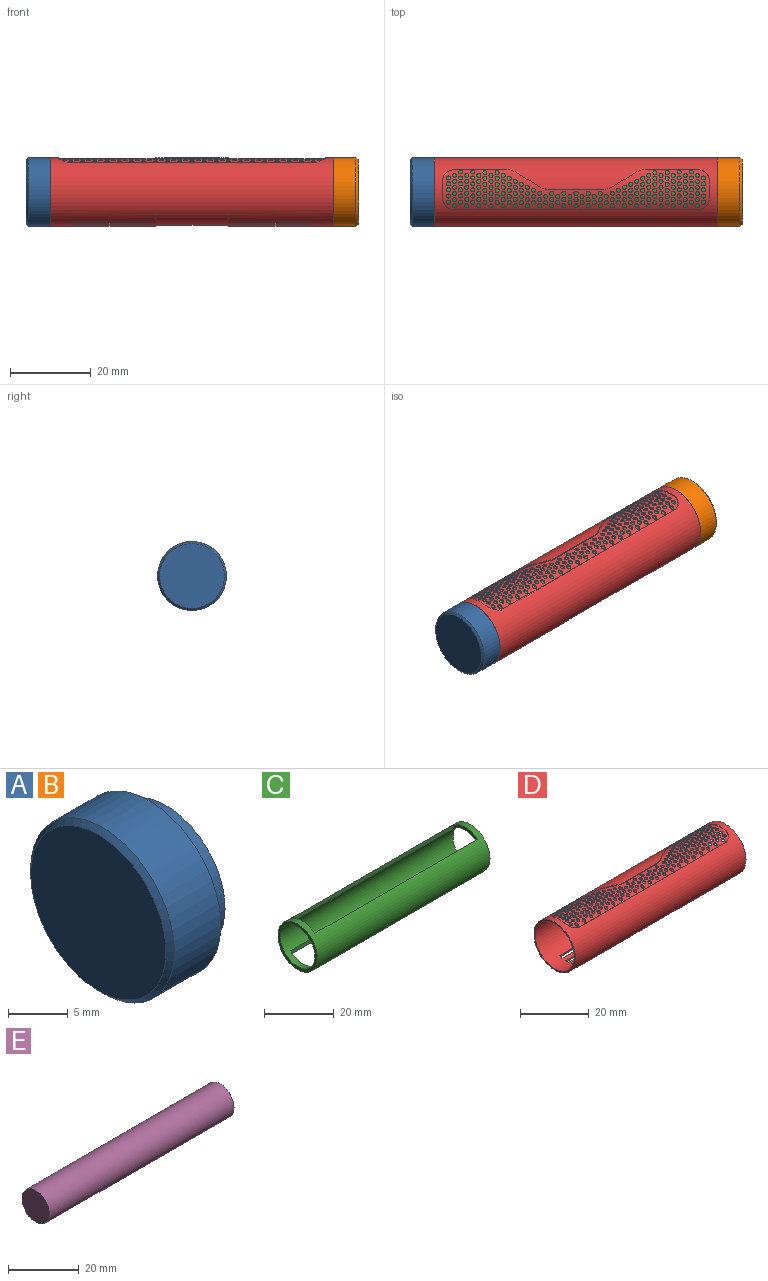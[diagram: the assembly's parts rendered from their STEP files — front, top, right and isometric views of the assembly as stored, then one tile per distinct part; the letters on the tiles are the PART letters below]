
ASSEMBLY  parts=5 mates=5
PART A: 8 faces, bbox 8x17x17 mm
  f0: cylinder r=5.5mm len=11mm, axis (-1,0,0), area 103.7mm2, adj f1,f6
  f1: plane 11x11mm, normal (1,0,0), area 95mm2, adj f0
  f2: cone r=8.25mm half-angle=45deg, axis (1,0,0), area 36.7mm2, adj f3,f4
  f3: cylinder r=8.5mm len=17mm, axis (1,0,0), area 293.7mm2, adj f2,f7
  f4: plane 16x16mm, normal (-1,0,0), area 201.1mm2, adj f2
  f5: cylinder r=7mm len=14mm, axis (1,0,0), area 88mm2, adj f6,f7
  f6: plane 14x14mm, normal (1,0,0), area 58.9mm2, adj f0,f5
  f7: plane 17x17mm, normal (1,0,0), area 73mm2, adj f3,f5
PART B: same geometry as A
PART C: 12 faces, bbox 70x16x16 mm
  f0: plane 10x3.1mm, normal (1,0,0), area 11mm2, adj f2,f4,f8,f10
  f1: plane 10x3.1mm, normal (1,0,0), area 11mm2, adj f3,f7,f8,f10
  f2: plane 66x1.35mm, normal (0,-1,0), area 88.8mm2, adj f0,f5,f8,f10
  f3: plane 66x1.35mm, normal (0,-1,0), area 88.8mm2, adj f1,f6,f8,f10
  f4: plane 66x1.35mm, normal (0,1,0), area 88.8mm2, adj f0,f5,f8,f10
  f5: plane 10x3.1mm, normal (-1,0,0), area 11mm2, adj f2,f4,f8,f10
  f6: plane 10x3.1mm, normal (-1,0,0), area 11mm2, adj f3,f7,f8,f10
  f7: plane 66x1.35mm, normal (0,1,0), area 88.8mm2, adj f1,f6,f8,f10
  f8: cylinder r=7mm len=70mm, axis (1,0,0), area 1608.5mm2, adj f0,f1,f2,f3,f4,f5,f6,f7
  f9: plane 16x16mm, normal (-1,0,0), area 47.1mm2, adj f8,f10
  f10: cylinder r=8mm len=70mm, axis (1,0,0), area 2092.7mm2, adj f0,f1,f2,f3,f4,f5,f6,f7
  f11: plane 16x16mm, normal (1,0,0), area 47.1mm2, adj f8,f10
PART D: 246 faces, bbox 70.2x17.2x17.2 mm
  f0: plane 13.02x3.2mm, normal (1,0,0), area 3.7mm2, adj f1,f2,f3,f244
  f1: plane 18x0.19mm, normal (0,0.64,-0.77), area 4.5mm2, adj f0,f2,f4,f244
  f2: cylinder r=8.25mm len=18mm, axis (1,0,0), area 259.2mm2, adj f0,f1,f3,f4
  f3: plane 18x0.19mm, normal (0,-0.64,-0.77), area 4.5mm2, adj f0,f2,f4,f244
  f4: plane 13.02x3.2mm, normal (-1,0,0), area 3.7mm2, adj f1,f2,f3,f244
  f5: plane 1x0.85mm, normal (1,0,0), area 0.5mm2, adj f6,f8,f128,f244
  f6: plane 20x0.52mm, normal (0,1,0), area 10.3mm2, adj f5,f7,f128,f244
  f7: plane 1x0.85mm, normal (-1,0,0), area 0.5mm2, adj f6,f8,f128,f244
  f8: plane 20x0.54mm, normal (0,-1,0), area 10.7mm2, adj f5,f7,f128,f244
  f9: plane 1x0.85mm, normal (1,0,0), area 0.5mm2, adj f10,f12,f128,f244
  f10: plane 20x0.54mm, normal (0,1,0), area 10.7mm2, adj f9,f11,f128,f244
  f11: plane 1x0.85mm, normal (-1,0,0), area 0.5mm2, adj f10,f12,f128,f244
  f12: plane 20x0.52mm, normal (0,-1,0), area 10.3mm2, adj f9,f11,f128,f244
  f13: plane 20x0.5mm, normal (0,1,0), area 10mm2, adj f14,f16,f128,f244
  f14: plane 1x0.52mm, normal (1,0,0), area 0.5mm2, adj f13,f15,f128,f244
  f15: plane 20x0.5mm, normal (0,-1,0), area 10mm2, adj f14,f16,f128,f244
  f16: plane 1x0.52mm, normal (-1,0,0), area 0.5mm2, adj f13,f15,f128,f244
  f17: plane 1x0.85mm, normal (-1,0,0), area 0.5mm2, adj f18,f20,f128,f244
  f18: plane 20x0.52mm, normal (0,1,0), area 10.3mm2, adj f17,f19,f128,f244
  f19: plane 1x0.85mm, normal (1,0,0), area 0.5mm2, adj f18,f20,f128,f244
  f20: plane 20x0.54mm, normal (0,-1,0), area 10.7mm2, adj f17,f19,f128,f244
  f21: plane 1x0.52mm, normal (1,0,0), area 0.5mm2, adj f22,f24,f128,f244
  f22: plane 20x0.5mm, normal (0,-1,0), area 10mm2, adj f21,f23,f128,f244
  f23: plane 1x0.52mm, normal (-1,0,0), area 0.5mm2, adj f22,f24,f128,f244
  f24: plane 20x0.5mm, normal (0,1,0), area 10mm2, adj f21,f23,f128,f244
  f25: plane 1x0.85mm, normal (-1,0,0), area 0.5mm2, adj f26,f28,f128,f244
  f26: plane 20x0.54mm, normal (0,1,0), area 10.7mm2, adj f25,f27,f128,f244
  f27: plane 1x0.85mm, normal (1,0,0), area 0.5mm2, adj f26,f28,f128,f244
  f28: plane 20x0.52mm, normal (0,-1,0), area 10.3mm2, adj f25,f27,f128,f244
  f29: cylinder r=0.5mm len=1mm, axis (0,0,-1), area 0.8mm2, adj f127,f128
  f30: cylinder r=0.5mm len=1mm, axis (0,0,-1), area 0.8mm2, adj f127,f128
  f31: cylinder r=0.5mm len=1mm, axis (0,0,-1), area 0.8mm2, adj f127,f128
  f32: cylinder r=0.5mm len=1mm, axis (0,0,-1), area 0.9mm2, adj f127,f128
  f33: cylinder r=0.5mm len=1mm, axis (0,0,-1), area 0.8mm2, adj f127,f128
  f34: cylinder r=0.5mm len=1mm, axis (0,0,-1), area 0.7mm2, adj f127,f128
  f35: cylinder r=0.5mm len=1mm, axis (0,0,-1), area 0.9mm2, adj f127,f128
  f36: cylinder r=0.5mm len=1mm, axis (0,0,-1), area 0.8mm2, adj f127,f128
  f37: cylinder r=0.5mm len=1mm, axis (0,0,-1), area 0.8mm2, adj f127,f128
  f38: cylinder r=0.5mm len=1mm, axis (0,0,-1), area 1mm2, adj f127,f128
  f39: cylinder r=0.5mm len=1mm, axis (0,0,-1), area 0.8mm2, adj f127,f128
  f40: cylinder r=0.5mm len=1mm, axis (0,0,-1), area 0.7mm2, adj f127,f128
  f41: cylinder r=0.5mm len=1mm, axis (0,0,-1), area 0.9mm2, adj f127,f128
  f42: cylinder r=0.5mm len=1mm, axis (0,0,-1), area 0.8mm2, adj f127,f128
  f43: cylinder r=0.5mm len=1mm, axis (0,0,-1), area 0.8mm2, adj f127,f128
  f44: cylinder r=0.5mm len=1mm, axis (0,0,-1), area 1mm2, adj f127,f128
  f45: cylinder r=0.5mm len=1mm, axis (0,0,-1), area 0.8mm2, adj f127,f128
  f46: cylinder r=0.5mm len=1mm, axis (0,0,-1), area 0.7mm2, adj f127,f128
  f47: cylinder r=0.5mm len=1mm, axis (0,0,-1), area 0.9mm2, adj f127,f128
  f48: cylinder r=0.5mm len=1mm, axis (0,0,-1), area 0.8mm2, adj f127,f128
  f49: cylinder r=0.5mm len=1mm, axis (0,0,-1), area 0.8mm2, adj f127,f128
  f50: cylinder r=0.5mm len=1mm, axis (0,0,-1), area 1mm2, adj f127,f128
  f51: cylinder r=0.5mm len=1mm, axis (0,0,-1), area 0.9mm2, adj f127,f128
  f52: cylinder r=0.5mm len=1mm, axis (0,0,-1), area 0.7mm2, adj f127,f128
  f53: cylinder r=0.5mm len=1mm, axis (0,0,-1), area 0.9mm2, adj f127,f128
  f54: cylinder r=0.5mm len=1mm, axis (0,0,-1), area 0.8mm2, adj f127,f128
  f55: cylinder r=0.5mm len=1mm, axis (0,0,-1), area 0.8mm2, adj f127,f128
  f56: cylinder r=0.5mm len=1mm, axis (0,0,-1), area 1mm2, adj f127,f128
  f57: cylinder r=0.5mm len=1mm, axis (0,0,-1), area 0.8mm2, adj f127,f128
  f58: cylinder r=0.5mm len=1mm, axis (0,0,-1), area 1mm2, adj f127,f128
  f59: cylinder r=0.5mm len=1mm, axis (0,0,-1), area 0.9mm2, adj f127,f128
  f60: cylinder r=0.5mm len=1mm, axis (0,0,-1), area 0.8mm2, adj f127,f128
  f61: cylinder r=0.5mm len=1mm, axis (0,0,-1), area 0.8mm2, adj f127,f128
  f62: cylinder r=0.5mm len=1mm, axis (0,0,-1), area 0.8mm2, adj f127,f128
  f63: cylinder r=0.5mm len=1mm, axis (0,0,-1), area 0.9mm2, adj f127,f128
  f64: cylinder r=0.5mm len=1mm, axis (0,0,-1), area 0.7mm2, adj f127,f128
  f65: cylinder r=0.5mm len=1mm, axis (0,0,-1), area 0.8mm2, adj f127,f128
  f66: cylinder r=0.5mm len=1mm, axis (0,0,-1), area 0.8mm2, adj f127,f128
  f67: cylinder r=0.5mm len=1mm, axis (0,0,-1), area 0.9mm2, adj f127,f128
  f68: cylinder r=0.5mm len=1mm, axis (0,0,-1), area 0.7mm2, adj f127,f128
  f69: cylinder r=0.5mm len=1mm, axis (0,0,-1), area 0.8mm2, adj f127,f128
  f70: cylinder r=0.5mm len=1mm, axis (0,0,-1), area 1mm2, adj f127,f128
  f71: cylinder r=0.5mm len=1mm, axis (0,0,-1), area 0.9mm2, adj f127,f128
  f72: cylinder r=0.5mm len=1mm, axis (0,0,-1), area 0.8mm2, adj f127,f128
  f73: cylinder r=0.5mm len=1mm, axis (0,0,-1), area 1mm2, adj f127,f128
  f74: cylinder r=0.5mm len=1mm, axis (0,0,-1), area 0.9mm2, adj f127,f128
  f75: cylinder r=0.5mm len=1mm, axis (0,0,-1), area 1mm2, adj f127,f128
  f76: cylinder r=0.5mm len=1mm, axis (0,0,-1), area 0.9mm2, adj f127,f128
  f77: cylinder r=0.5mm len=1mm, axis (0,0,-1), area 0.8mm2, adj f127,f128
  f78: cylinder r=0.5mm len=1mm, axis (0,0,-1), area 0.4mm2, adj f127,f128,f178
  f79: cylinder r=0.5mm len=1mm, axis (0,0,-1), area 0.4mm2, adj f127,f128,f177
  f80: cylinder r=0.5mm len=1mm, axis (0,0,-1), area 0.5mm2, adj f127,f128,f176
  f81: cylinder r=0.5mm len=1mm, axis (0,0,-1), area 0.9mm2, adj f127,f128
  f82: cylinder r=0.5mm len=1mm, axis (0,0,-1), area 0.9mm2, adj f127,f128
  f83: cylinder r=0.5mm len=1mm, axis (0,0,-1), area 0.8mm2, adj f127,f128
  f84: cylinder r=0.5mm len=1mm, axis (0,0,-1), area 0.9mm2, adj f127,f128
  f85: cylinder r=0.5mm len=1mm, axis (0,0,-1), area 0.8mm2, adj f127,f128
  f86: cylinder r=0.5mm len=1mm, axis (0,0,-1), area 0.9mm2, adj f127,f128
  f87: cylinder r=0.5mm len=1mm, axis (0,0,-1), area 0.9mm2, adj f127,f128
  f88: cylinder r=0.5mm len=1mm, axis (0,0,-1), area 0.8mm2, adj f127,f128
  f89: cylinder r=0.5mm len=1mm, axis (0,0,-1), area 0.9mm2, adj f127,f128
  f90: cylinder r=0.5mm len=1mm, axis (0,0,-1), area 1mm2, adj f127,f128
  f91: cylinder r=0.5mm len=1mm, axis (0,0,-1), area 0.9mm2, adj f127,f128
  f92: cylinder r=0.5mm len=1mm, axis (0,0,-1), area 0.8mm2, adj f127,f128
  f93: cylinder r=0.5mm len=1mm, axis (0,0,-1), area 0.9mm2, adj f127,f128
  f94: cylinder r=0.5mm len=1mm, axis (0,0,-1), area 1mm2, adj f127,f128
  f95: cylinder r=0.5mm len=1mm, axis (0,0,-1), area 0.9mm2, adj f127,f128
  f96: cylinder r=0.5mm len=1mm, axis (0,0,-1), area 0.9mm2, adj f127,f128
  f97: cylinder r=0.5mm len=1mm, axis (0,0,-1), area 0.8mm2, adj f127,f128
  f98: cylinder r=0.5mm len=1mm, axis (0,0,-1), area 0.9mm2, adj f127,f128
  f99: cylinder r=0.5mm len=1mm, axis (0,0,-1), area 0.9mm2, adj f127,f128
  f100: cylinder r=0.5mm len=1mm, axis (0,0,-1), area 0.7mm2, adj f127,f128
  f101: cylinder r=0.5mm len=1mm, axis (0,0,-1), area 0.8mm2, adj f127,f128
  f102: cylinder r=0.5mm len=1mm, axis (0,0,-1), area 0.9mm2, adj f127,f128
  f103: cylinder r=0.5mm len=1mm, axis (0,0,-1), area 0.8mm2, adj f127,f128
  f104: cylinder r=0.5mm len=1mm, axis (0,0,-1), area 0.9mm2, adj f127,f128
  f105: cylinder r=0.5mm len=1mm, axis (0,0,-1), area 0.8mm2, adj f127,f128
  f106: cylinder r=0.5mm len=1mm, axis (0,0,-1), area 1mm2, adj f127,f128
  f107: cylinder r=0.5mm len=1mm, axis (0,0,-1), area 0.9mm2, adj f127,f128
  f108: cylinder r=0.5mm len=1mm, axis (0,0,-1), area 0.9mm2, adj f127,f128
  f109: cylinder r=0.5mm len=1mm, axis (0,0,-1), area 0.8mm2, adj f127,f128
  f110: cylinder r=0.5mm len=1mm, axis (0,0,-1), area 0.9mm2, adj f127,f128
  f111: cylinder r=0.5mm len=1mm, axis (0,0,-1), area 0.8mm2, adj f127,f128
  f112: cylinder r=0.5mm len=1mm, axis (0,0,-1), area 1mm2, adj f127,f128
  f113: cylinder r=0.5mm len=1mm, axis (0,0,-1), area 0.9mm2, adj f127,f128
  f114: cylinder r=0.5mm len=1mm, axis (0,0,-1), area 0.9mm2, adj f127,f128
  f115: cylinder r=0.5mm len=1mm, axis (0,0,-1), area 0.8mm2, adj f127,f128
  f116: cylinder r=0.5mm len=1mm, axis (0,0,-1), area 0.8mm2, adj f127,f128
  f117: cylinder r=0.5mm len=1mm, axis (0,0,-1), area 0.8mm2, adj f127,f128
  f118: cylinder r=0.5mm len=1mm, axis (0,0,-1), area 1mm2, adj f127,f128
  f119: cylinder r=0.5mm len=1mm, axis (0,0,-1), area 0.9mm2, adj f127,f128
  f120: cylinder r=0.5mm len=1mm, axis (0,0,-1), area 0.9mm2, adj f127,f128
  f121: cylinder r=0.5mm len=1mm, axis (0,0,-1), area 0.8mm2, adj f127,f128
  f122: cylinder r=0.5mm len=1mm, axis (0,0,-1), area 0.8mm2, adj f127,f128
  f123: cylinder r=0.5mm len=1mm, axis (0,0,-1), area 0.8mm2, adj f127,f128
  f124: cylinder r=0.5mm len=1mm, axis (0,0,-1), area 1mm2, adj f127,f128
  f125: cylinder r=0.5mm len=1mm, axis (0,0,-1), area 0.9mm2, adj f127,f128
  f126: cylinder r=0.5mm len=1mm, axis (0,0,-1), area 0.8mm2, adj f127,f128
  f127: cylinder r=8.25mm len=66mm, axis (-1,0,0), area 409.4mm2, adj f29,f30,f31,f32,f33,f34,f35,f36
  f128: cylinder r=8mm len=70mm, axis (1,0,0), area 3233.7mm2, adj f5,f6,f7,f8,f9,f10,f11,f12
  f129: cylinder r=0.5mm len=1mm, axis (0,0,1), area 0.8mm2, adj f127,f128
  f130: cylinder r=0.5mm len=1mm, axis (0,0,1), area 0.8mm2, adj f127,f128
  f131: cylinder r=0.5mm len=1mm, axis (0,0,1), area 0.9mm2, adj f127,f128
  f132: cylinder r=0.5mm len=1mm, axis (0,0,1), area 1mm2, adj f127,f128
  f133: cylinder r=0.5mm len=1mm, axis (0,0,1), area 0.8mm2, adj f127,f128
  f134: cylinder r=0.5mm len=1mm, axis (0,0,1), area 0.9mm2, adj f127,f128
  f135: cylinder r=0.5mm len=1mm, axis (0,0,1), area 0.8mm2, adj f127,f128
  f136: cylinder r=0.5mm len=1mm, axis (0,0,1), area 0.9mm2, adj f127,f128
  f137: cylinder r=0.5mm len=1mm, axis (0,0,1), area 0.9mm2, adj f127,f128
  f138: cylinder r=0.5mm len=1mm, axis (0,0,1), area 1mm2, adj f127,f128
  f139: cylinder r=0.5mm len=1mm, axis (0,0,1), area 0.8mm2, adj f127,f128
  f140: cylinder r=0.5mm len=1mm, axis (0,0,1), area 0.8mm2, adj f127,f128
  f141: cylinder r=0.5mm len=1mm, axis (0,0,1), area 0.8mm2, adj f127,f128
  f142: cylinder r=0.5mm len=1mm, axis (0,0,1), area 0.8mm2, adj f127,f128
  f143: cylinder r=0.5mm len=1mm, axis (0,0,1), area 0.9mm2, adj f127,f128
  f144: cylinder r=0.5mm len=1mm, axis (0,0,1), area 1mm2, adj f127,f128
  f145: cylinder r=0.5mm len=1mm, axis (0,0,1), area 0.8mm2, adj f127,f128
  f146: cylinder r=0.5mm len=1mm, axis (0,0,1), area 0.8mm2, adj f127,f128
  f147: cylinder r=0.5mm len=1mm, axis (0,0,1), area 0.8mm2, adj f127,f128
  f148: cylinder r=0.5mm len=1mm, axis (0,0,1), area 0.8mm2, adj f127,f128
  f149: cylinder r=0.5mm len=1mm, axis (0,0,1), area 0.9mm2, adj f127,f128
  f150: cylinder r=0.5mm len=1mm, axis (0,0,1), area 1mm2, adj f127,f128
  f151: cylinder r=0.5mm len=1mm, axis (0,0,1), area 0.8mm2, adj f127,f128
  f152: cylinder r=0.5mm len=1mm, axis (0,0,1), area 0.8mm2, adj f127,f128
  f153: cylinder r=0.5mm len=1mm, axis (0,0,1), area 0.8mm2, adj f127,f128
  f154: cylinder r=0.5mm len=1mm, axis (0,0,1), area 0.8mm2, adj f127,f128
  f155: cylinder r=0.5mm len=1mm, axis (0,0,1), area 0.8mm2, adj f127,f128
  f156: cylinder r=0.5mm len=1mm, axis (0,0,1), area 0.7mm2, adj f127,f128
  f157: cylinder r=0.5mm len=1mm, axis (0,0,1), area 0.8mm2, adj f127,f128
  f158: cylinder r=0.5mm len=1mm, axis (0,0,1), area 0.8mm2, adj f127,f128
  f159: cylinder r=0.5mm len=1mm, axis (0,0,1), area 0.8mm2, adj f127,f128
  f160: cylinder r=0.5mm len=1mm, axis (0,0,1), area 0.8mm2, adj f127,f128
  f161: cylinder r=0.5mm len=1mm, axis (0,0,1), area 0.9mm2, adj f127,f128
  f162: cylinder r=0.5mm len=1mm, axis (0,0,1), area 1mm2, adj f127,f128
  f163: cylinder r=0.5mm len=1mm, axis (0,0,1), area 0.9mm2, adj f127,f128
  f164: cylinder r=0.5mm len=1mm, axis (0,0,1), area 0.8mm2, adj f127,f128
  f165: cylinder r=0.5mm len=1mm, axis (0,0,1), area 0.9mm2, adj f127,f128
  f166: cylinder r=0.5mm len=1mm, axis (0,0,1), area 1mm2, adj f127,f128
  f167: cylinder r=0.5mm len=1mm, axis (0,0,1), area 0.9mm2, adj f127,f128
  f168: cylinder r=0.5mm len=1mm, axis (0,0,1), area 0.8mm2, adj f127,f128
  f169: cylinder r=0.5mm len=1mm, axis (0,0,1), area 0.9mm2, adj f127,f128
  f170: cylinder r=0.5mm len=1mm, axis (0,0,1), area 0.8mm2, adj f127,f128
  f171: cylinder r=0.5mm len=1mm, axis (0,0,1), area 0.8mm2, adj f127,f128
  f172: cylinder r=0.5mm len=1mm, axis (0,0,1), area 0.9mm2, adj f127,f128
  f173: cylinder r=0.5mm len=1mm, axis (0,0,1), area 0.8mm2, adj f127,f128
  f174: cylinder r=0.5mm len=1mm, axis (0,0,1), area 0.8mm2, adj f127,f128
  f175: cylinder r=0.5mm len=1mm, axis (0,0,1), area 0.8mm2, adj f127,f128
  f176: cylinder r=0.5mm len=1mm, axis (0,0,1), area 0.5mm2, adj f80,f127,f128
  f177: cylinder r=0.5mm len=1mm, axis (0,0,1), area 0.4mm2, adj f79,f127,f128
  f178: cylinder r=0.5mm len=1mm, axis (0,0,1), area 0.4mm2, adj f78,f127,f128
  f179: cylinder r=0.5mm len=1mm, axis (0,0,1), area 0.8mm2, adj f127,f128
  f180: cylinder r=0.5mm len=1mm, axis (0,0,1), area 0.9mm2, adj f127,f128
  f181: cylinder r=0.5mm len=1mm, axis (0,0,1), area 1mm2, adj f127,f128
  f182: cylinder r=0.5mm len=1mm, axis (0,0,1), area 0.8mm2, adj f127,f128
  f183: cylinder r=0.5mm len=1mm, axis (0,0,1), area 1mm2, adj f127,f128
  f184: cylinder r=0.5mm len=1mm, axis (0,0,1), area 0.8mm2, adj f127,f128
  f185: cylinder r=0.5mm len=1mm, axis (0,0,1), area 0.9mm2, adj f127,f128
  f186: cylinder r=0.5mm len=1mm, axis (0,0,1), area 1mm2, adj f127,f128
  f187: cylinder r=0.5mm len=1mm, axis (0,0,1), area 0.8mm2, adj f127,f128
  f188: cylinder r=0.5mm len=1mm, axis (0,0,1), area 0.7mm2, adj f127,f128
  f189: cylinder r=0.5mm len=1mm, axis (0,0,1), area 0.9mm2, adj f127,f128
  f190: cylinder r=0.5mm len=1mm, axis (0,0,1), area 0.8mm2, adj f127,f128
  f191: cylinder r=0.5mm len=1mm, axis (0,0,1), area 0.8mm2, adj f127,f128
  f192: cylinder r=0.5mm len=1mm, axis (0,0,1), area 0.7mm2, adj f127,f128
  f193: cylinder r=0.5mm len=1mm, axis (0,0,1), area 0.9mm2, adj f127,f128
  f194: cylinder r=0.5mm len=1mm, axis (0,0,1), area 0.8mm2, adj f127,f128
  f195: cylinder r=0.5mm len=1mm, axis (0,0,1), area 0.8mm2, adj f127,f128
  f196: cylinder r=0.5mm len=1mm, axis (0,0,1), area 0.8mm2, adj f127,f128
  f197: cylinder r=0.5mm len=1mm, axis (0,0,1), area 0.9mm2, adj f127,f128
  f198: cylinder r=0.5mm len=1mm, axis (0,0,1), area 1mm2, adj f127,f128
  f199: cylinder r=0.5mm len=1mm, axis (0,0,1), area 0.8mm2, adj f127,f128
  f200: cylinder r=0.5mm len=1mm, axis (0,0,1), area 0.9mm2, adj f127,f128
  f201: cylinder r=0.5mm len=1mm, axis (0,0,1), area 0.8mm2, adj f127,f128
  f202: cylinder r=0.5mm len=1mm, axis (0,0,1), area 0.8mm2, adj f127,f128
  f203: cylinder r=0.5mm len=1mm, axis (0,0,1), area 0.8mm2, adj f127,f128
  f204: cylinder r=0.5mm len=1mm, axis (0,0,1), area 0.7mm2, adj f127,f128
  f205: cylinder r=0.5mm len=1mm, axis (0,0,1), area 0.8mm2, adj f127,f128
  f206: cylinder r=0.5mm len=1mm, axis (0,0,1), area 0.9mm2, adj f127,f128
  f207: cylinder r=0.5mm len=1mm, axis (0,0,1), area 0.8mm2, adj f127,f128
  f208: cylinder r=0.5mm len=1mm, axis (0,0,1), area 0.8mm2, adj f127,f128
  f209: cylinder r=0.5mm len=1mm, axis (0,0,1), area 0.8mm2, adj f127,f128
  f210: cylinder r=0.5mm len=1mm, axis (0,0,1), area 0.7mm2, adj f127,f128
  f211: cylinder r=0.5mm len=1mm, axis (0,0,1), area 0.8mm2, adj f127,f128
  f212: cylinder r=0.5mm len=1mm, axis (0,0,1), area 1mm2, adj f127,f128
  f213: cylinder r=0.5mm len=1mm, axis (0,0,1), area 0.8mm2, adj f127,f128
  f214: cylinder r=0.5mm len=1mm, axis (0,0,1), area 0.8mm2, adj f127,f128
  f215: cylinder r=0.5mm len=1mm, axis (0,0,1), area 0.8mm2, adj f127,f128
  f216: cylinder r=0.5mm len=1mm, axis (0,0,1), area 0.7mm2, adj f127,f128
  f217: cylinder r=0.5mm len=1mm, axis (0,0,1), area 0.8mm2, adj f127,f128
  f218: cylinder r=0.5mm len=1mm, axis (0,0,1), area 1mm2, adj f127,f128
  f219: cylinder r=0.5mm len=1mm, axis (0,0,1), area 0.8mm2, adj f127,f128
  f220: cylinder r=0.5mm len=1mm, axis (0,0,1), area 0.8mm2, adj f127,f128
  f221: cylinder r=0.5mm len=1mm, axis (0,0,1), area 0.9mm2, adj f127,f128
  f222: cylinder r=0.5mm len=1mm, axis (0,0,1), area 0.7mm2, adj f127,f128
  f223: cylinder r=0.5mm len=1mm, axis (0,0,1), area 0.9mm2, adj f127,f128
  f224: cylinder r=0.5mm len=1mm, axis (0,0,1), area 0.9mm2, adj f127,f128
  f225: cylinder r=0.5mm len=1mm, axis (0,0,1), area 0.8mm2, adj f127,f128
  f226: cylinder r=0.5mm len=1mm, axis (0,0,1), area 0.9mm2, adj f127,f128
  f227: cylinder r=4mm len=2.12mm, axis (0,0,1), area 0.5mm2, adj f127,f228,f242,f244
  f228: plane 6.29x4.01mm, normal (0.53,-0.85,0), area 1.9mm2, adj f127,f227,f229,f244
  f229: cylinder r=4mm len=2.12mm, axis (0,0,1), area 0.7mm2, adj f127,f228,f230,f244
  f230: plane 12.85x0.31mm, normal (0,-1,0), area 4mm2, adj f127,f229,f231,f244
  f231: cylinder r=3mm len=3mm, axis (0,0,1), area 1.3mm2, adj f127,f230,f232,f244
  f232: plane 4x0.5mm, normal (-1,0,0), area 1mm2, adj f127,f231,f233,f244
  f233: cylinder r=3mm len=3mm, axis (0,0,1), area 1.4mm2, adj f127,f232,f234,f244
  f234: plane 60x0.31mm, normal (0,1,0), area 18.7mm2, adj f127,f233,f235,f244
  f235: cylinder r=3mm len=3mm, axis (0,0,1), area 1.3mm2, adj f127,f234,f236,f244
  f236: plane 4x0.5mm, normal (1,0,0), area 1mm2, adj f127,f235,f237,f244
  f237: cylinder r=3mm len=3mm, axis (0,0,1), area 1.4mm2, adj f127,f236,f238,f244
  f238: plane 12.85x0.31mm, normal (0,-1,0), area 4mm2, adj f127,f237,f239,f244
  f239: cylinder r=4mm len=2.12mm, axis (0,0,1), area 0.7mm2, adj f127,f238,f240,f244
  f240: plane 6.29x4.01mm, normal (-0.53,-0.85,0), area 1.9mm2, adj f127,f239,f241,f244
  f241: cylinder r=4mm len=2.12mm, axis (0,0,1), area 0.5mm2, adj f127,f240,f242,f244
  f242: plane 13.71x0.25mm, normal (0,-1,0), area 3.4mm2, adj f127,f227,f241,f244
  f243: plane 17x17mm, normal (-1,0,0), area 25.9mm2, adj f128,f244
  f244: cylinder r=8.5mm len=70mm, axis (1,0,0), area 2780.4mm2, adj f0,f1,f3,f4,f5,f6,f7,f8
  f245: plane 17x17mm, normal (1,0,0), area 25.9mm2, adj f128,f244
PART E: 3 faces, bbox 74x11x11 mm
  f0: plane 11x11mm, normal (-1,0,0), area 95mm2, adj f1
  f1: cylinder r=5.5mm len=74mm, axis (1,0,0), area 2557.3mm2, adj f0,f2
  f2: plane 11x11mm, normal (1,0,0), area 95mm2, adj f1
PLACE A rot(axis=(-1,0,0),94.5deg) t=(-55.32,1,5.6)mm
PLACE B rot(axis=(0,-0.68,0.73),180deg) t=(26.68,1,5.6)mm
PLACE C rot(axis=(1,0,0),85.5deg) t=(-14.32,1,5.6)mm
PLACE D rot(axis=(-1,0,0),4.5deg) t=(-14.32,1,5.6)mm
PLACE E rot(axis=(-1,0,0),4.5deg) t=(-15.32,1,5.6)mm
MATE cylindrical E.f1 <-> A.f0  axis (1,0,0) through (-15.32,1,5.6)mm
MATE fastened C.f8 <-> B.f0  axis (1,0,0) through (20.68,1,5.6)mm
MATE fastened B.f0 <-> D.f2  axis (-1,0,0) through (20.68,1,5.6)mm
MATE fastened C.f8 <-> A.f0  axis (-1,0,0) through (-49.32,1,5.6)mm
MATE fastened E.f1 <-> B.f0  axis (1,0,0) through (21.68,1,5.6)mm
